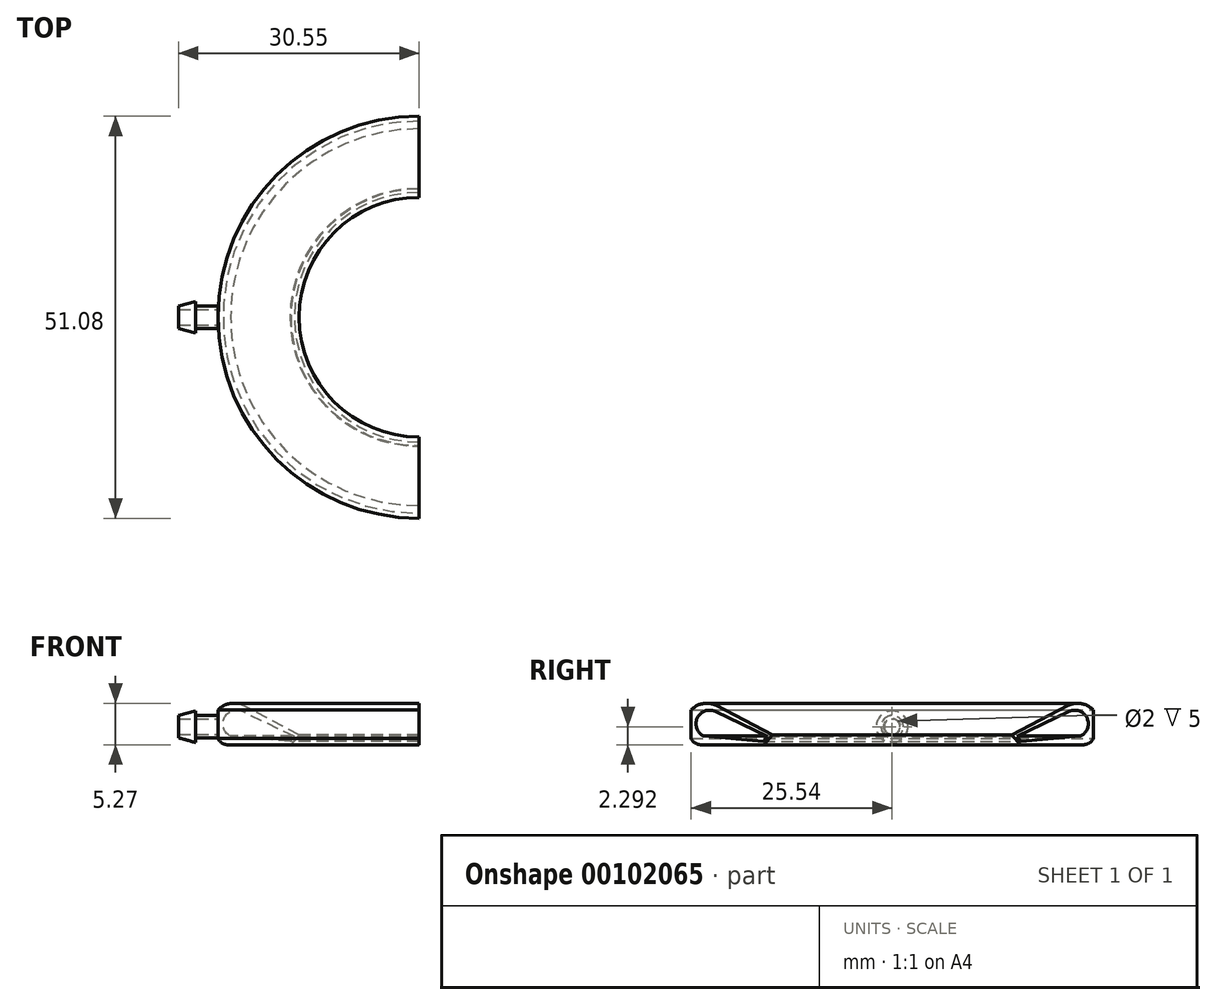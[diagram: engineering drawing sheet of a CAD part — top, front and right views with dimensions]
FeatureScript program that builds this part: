
annotation { "Feature Type Name" : "Feature", "Feature Type Description" : "" }
export const myFeature = defineFeature(function(context is Context, id is Id, definition is map)
    precondition{}
    {
        {
            var Q0;
            Q0=qCreatedBy(makeId("Front.planeOp"),FACE);
            var sketch = newSketch(context, id + "F0", { "sketchPlane" : qUnion([Q0])});
            skLineSegment(sketch, "E0", {"start": v(15, 0) * mm, "end": v(16.29, 0) * mm});
            skLineSegment(sketch, "E1", {"start": v(15.23, 1.25) * mm, "end": v(22.32, 4.96) * mm});
            skLineSegment(sketch, "E2", {"start": v(16.29, 0) * mm, "end": v(24.29, 0) * mm});
            skLineSegment(sketch, "E3", {"start": v(15.53, 0.9) * mm, "end": v(22.43, 4.22) * mm});
            skLineSegment(sketch, "E4", {"start": v(15.97, 0.38) * mm, "end": v(23.94, 1.1) * mm});
            skArc(sketch, "E5", {"start": v(23.94, 1.1) * mm, "mid": v(24.74, 3.4) * mm, "end": v(22.43, 4.22) * mm});
            skLineSegment(sketch, "E6", {"start": v(0, 0) * mm, "end": v(0, 3.69) * mm});
            skLineSegment(sketch, "E7", {"start": v(15.53, 0.9) * mm, "end": v(15.23, 1.25) * mm});
            skLineSegment(sketch, "E8", {"start": v(15.97, 0.38) * mm, "end": v(16.29, 0) * mm});
            skLineSegment(sketch, "E9", {"start": v(25.54, 4.4) * mm, "end": v(25.54, 0.77) * mm});
            skArc(sketch, "E10", {"start": v(25.54, 4.4) * mm, "mid": v(24.03, 5.23) * mm, "end": v(22.32, 4.96) * mm});
            skArc(sketch, "E11", {"start": v(24.29, 0) * mm, "mid": v(25.02, 0.2) * mm, "end": v(25.54, 0.77) * mm});
            skLineSegment(sketch, "E12", {"start": v(15.49, 0.95) * mm, "end": v(15.97, 0.38) * mm});
            skLineSegment(sketch, "E13", {"start": v(16.37, 0.41) * mm, "end": v(15.84, 1.04) * mm});
            skSolve(sketch);
        }
        {
            var Q0;
            {var subQ0=sQuery(id+"F0.wireOp",EDGE,"E1");Q0=makeQuery(id+"F0.imprint","IMPRINT",FACE,{"disambiguationData":[TD([[makeQuery(id+"F0.imprint","IMPRINT",EDGE,{"derivedFrom":subQ0}),-1.0]])]});}
            var Q1;
            {var subQ5=sQuery(id+"F0.wireOp",EDGE,"URcUcSot-s3Vu-5bZ4-lVOO-fd6WexAXXO60");Q1=makeQuery(id+"F0.imprint","IMPRINT",FACE,{"disambiguationData":[TD([[makeQuery(id+"F0.imprint","IMPRINT",EDGE,{"derivedFrom":subQ5}),-1.0]])]});}
            var Q2;
            {var subQ3=sQuery(id+"F0.wireOp",EDGE,"E13");Q2=makeQuery(id+"F0.imprint","IMPRINT",FACE,{"disambiguationData":[TD([[makeQuery(id+"F0.imprint","IMPRINT",EDGE,{"derivedFrom":subQ3}),1.0]])]});}
            var Q3;
            Q3=sQuery(id+"F0.wireOp",EDGE,"E6");
            revolve(context, id + "F1", {"entities" : qUnion([Q0, Q1, Q2]), "axis" : qUnion([Q3]), "revolveType" : RevolveType.FULL});
        }
        {
            var Q0;
            Q0=qCreatedBy(makeId("Front.planeOp"),FACE);
            var sketch = newSketch(context, id + "F2", { "sketchPlane" : qUnion([Q0])});
            skLineSegment(sketch, "E14", {"start": v(-25.54, 2.3) * mm, "end": v(-27.05, 2.3) * mm});
            skLineSegment(sketch, "E15", {"start": v(-28.4, 3.7) * mm, "end": v(-28.4, 4.3) * mm});
            skLineSegment(sketch, "E16", {"start": v(-28.4, 4.3) * mm, "end": v(-30.55, 3.7) * mm});
            skLineSegment(sketch, "E17", {"start": v(-30.55, 3.7) * mm, "end": v(-30.55, 3.3) * mm});
            skLineSegment(sketch, "E18", {"start": v(-30.55, 3.3) * mm, "end": v(-25.55, 3.3) * mm});
            skLineSegment(sketch, "E19", {"start": v(-25.55, 3.3) * mm, "end": v(-25.4, 3.7) * mm});
            skLineSegment(sketch, "E20", {"start": v(-25.4, 3.7) * mm, "end": v(-28.4, 3.7) * mm});
            skSolve(sketch);
        }
        {
            var Q0;
            Q0=qSketchRegion(id+"F2",true);
            var Q1;
            Q1=sQuery(id+"F2.wireOp",EDGE,"E14");
            revolve(context, id + "F3", {"operationType" : NewBodyOperationType.ADD, "entities" : qUnion([Q0]), "axis" : qUnion([Q1]), "revolveType" : RevolveType.FULL});
        }
        {
            var Q0;
            Q0=qCreatedBy(makeId("Right.planeOp"),FACE);
            var sketch = newSketch(context, id + "F4", { "sketchPlane" : qUnion([Q0])});
            skLineSegment(sketch, "E21.bottom", {"start": v(-25.71, 6.59) * mm, "end": v(25.71, 6.59) * mm});
            skLineSegment(sketch, "E21.top", {"start": v(-25.71, -1.27) * mm, "end": v(25.71, -1.27) * mm});
            skLineSegment(sketch, "E21.left", {"start": v(-25.71, 6.59) * mm, "end": v(-25.71, -1.27) * mm});
            skLineSegment(sketch, "E21.right", {"start": v(25.71, 6.59) * mm, "end": v(25.71, -1.27) * mm});
            skSolve(sketch);
        }
        {
            var Q0;
            Q0 = qSketchRegion(id + "F4", true);
            extrude(context, id + "F5", {"entities" : qUnion([Q0]), "operationType" : NewBodyOperationType.REMOVE, "depth" : 26 * mm});
        }
    });
